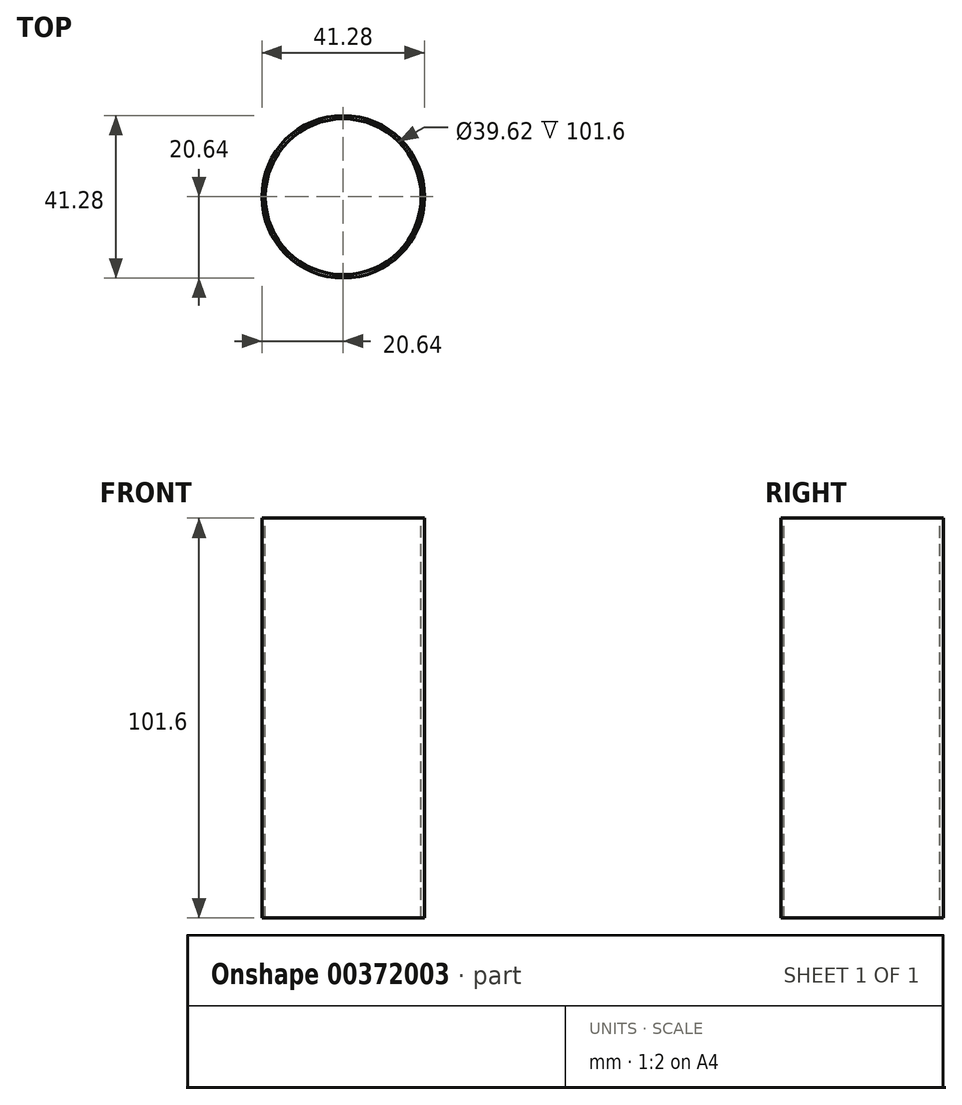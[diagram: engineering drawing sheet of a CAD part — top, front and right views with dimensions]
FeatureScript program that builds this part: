
annotation { "Feature Type Name" : "Feature", "Feature Type Description" : "" }
export const myFeature = defineFeature(function(context is Context, id is Id, definition is map)
    precondition{}
    {
        {
            var Q0;
            Q0=qCreatedBy(makeId("Front.planeOp"),FACE);
            var sketch = newSketch(context, id + "F0", { "sketchPlane" : qUnion([Q0])});
            skLineSegment(sketch, "E0", {"start": v(0, 0) * mm, "end": v(-20.64, 0) * mm});
            skLineSegment(sketch, "E1", {"start": v(0, 0) * mm, "end": v(0, 101.6) * mm});
            skLineSegment(sketch, "E2", {"start": v(20.49, 101.6) * mm, "end": v(-20.64, 101.6) * mm});
            skLineSegment(sketch, "E3", {"start": v(-20.64, 101.6) * mm, "end": v(-20.64, 0) * mm});
            skSolve(sketch);
        }
        {
            var Q0;
            Q0=makeQuery(id+"F0.imprint","IMPRINT",FACE,{"disambiguationData":[TD([[makeQuery(id+"F0.imprint","IMPRINT",EDGE,{"derivedFrom":sQuery(id+"F0.wireOp",EDGE,"E0")}),-1.0]])]});
            var Q1;
            Q1=sQuery(id+"F0.wireOp",EDGE,"E1");
            revolve(context, id + "F1", {"entities" : qUnion([Q0]), "axis" : qUnion([Q1]), "revolveType" : RevolveType.FULL});
        }
        {
            var Q0;
            Q0=makeQuery(id+"F1.opRevolve","SWEPT_FACE",FACE,{"disambiguationData":[OSD([sQuery(id+"F0.wireOp",EDGE,"E2")])]});
            var sketch = newSketch(context, id + "F2", { "sketchPlane" : qUnion([Q0])});
            skCircle(sketch, "E4", {"center": v(0, 0) * mm, "radius": 19.81 * mm});
            skSolve(sketch);
        }
        {
            var Q0;
            Q0=sQuery(id+"F2.wireOp",VERTEX,"E4.center");
            var Q1;
            Q1=makeQuery(id+"F1.opRevolve","SWEPT_BODY",BODY,{"disambiguationData":[OSD([sQuery(id+"F0.wireOp",EDGE,"E0"),sQuery(id+"F0.wireOp",EDGE,"E1"),sQuery(id+"F0.wireOp",EDGE,"E2"),sQuery(id+"F0.wireOp",EDGE,"E3")])]});
            hole(context, id + "F3", {"style" : HoleStyle.SIMPLE, "endStyle" : HoleEndStyle.THROUGH, "holeDiameter" : 39.62 * mm, "isTappedThrough" : true, "tappedDepth" : 12.7 * mm, "tapClearance" : 3, "locations" : qUnion([Q0]), "scope" : qUnion([Q1])});
        }
    });
